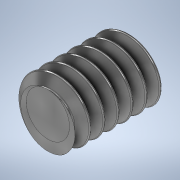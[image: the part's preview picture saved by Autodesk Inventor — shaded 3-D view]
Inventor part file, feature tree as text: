
AUTODESK INVENTOR PART (.ipt)
format: ipt  version: 2020 (Build 240168000, 168)  size: 585,728 bytes
history: native  units: in
note: dims shown in document units (in); Inventor stores cm internally (conversion verified against a paired STEP export)
features: sketch x5, extrude x2, fillet x2, revolve x2, thread x1, helix x1
ambient origin geometry x8: Origin, YZ Plane, XZ Plane, XY Plane, X Axis, Y Axis, Z Axis, Center Point
bodies: Solid1 (feature_tree), Solid2 (feature_tree)
feature tree (13):
  extrude  "Extrusion1"  Depth=0.25in TaperAngle=0.0deg
  thread  "Thread1"  [1 undecoded]
  fillet  "Fillet1"  Radius=0.02in
  fillet  "Fillet2"  Radius=0.04in
  extrude  "Extrusion2"  Depth=0.0185in
  revolve  "Revolution1"  [1 undecoded]
  revolve  "Revolution2"  [1 undecoded]
  helix  "Coil1"  [1 undecoded]
  sketch  "Sketch1"  dims[d0=0.19in d1=0.25in d2=0.0in d3=0.25in d4=0.0in d5=0.02in d6=0.04in]
  sketch  "Sketch2"  dims[d7=0.2in d8=0.0185in]
  sketch  "Sketch3"  dims[d9=0.03in d10=0.0in d11=0.3779in d12=0.0067in d13=0.0067in]
  sketch  "Sketch4"  dims[d16=0.0417in d18=0.3779in d20=0.0in]
  sketch  "Sketch5"  dims[d21=0.0in d22=0.0417in d23=0.3333in d24=0.3937in d25=0.0in d26=0.0in d27=0.0in d28=0.0in d29=0.0in]
note: 4 required parameter values undecoded (feature->parameter linkage not recoverable at this tier; creation-order binding heuristic only, values carry confidence <= 0.55)